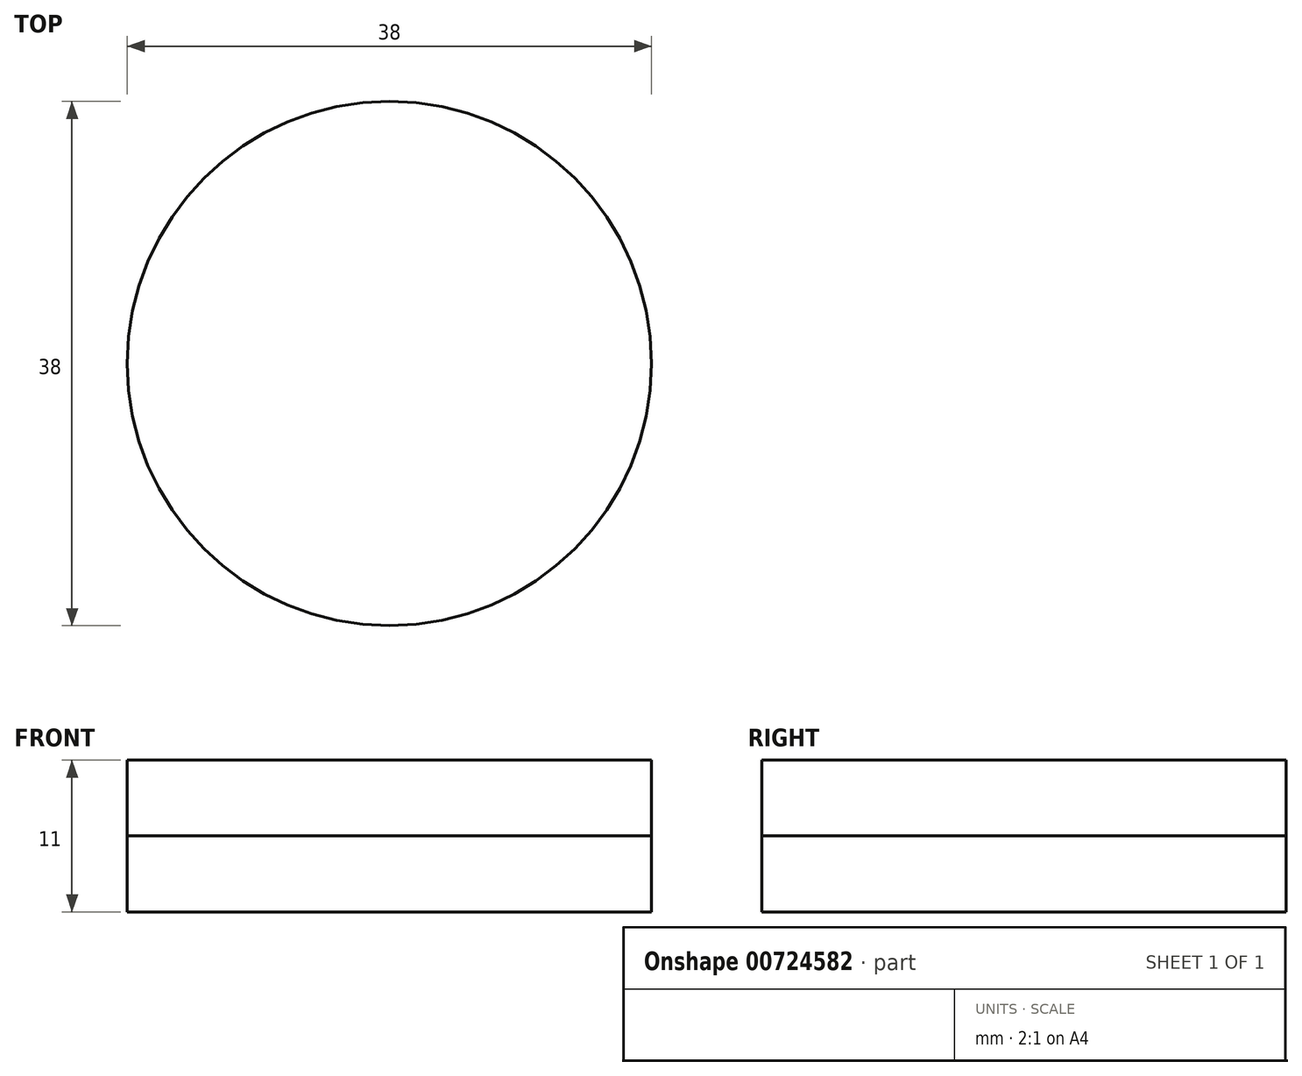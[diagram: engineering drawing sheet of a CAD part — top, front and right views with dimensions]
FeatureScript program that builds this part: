
annotation { "Feature Type Name" : "Feature", "Feature Type Description" : "" }
export const myFeature = defineFeature(function(context is Context, id is Id, definition is map)
    precondition{}
    {
        {
            var Q0;
            Q0=qCreatedBy(makeId("Top.planeOp"),FACE);
            var sketch = newSketch(context, id + "F0", { "sketchPlane" : qUnion([Q0])});
            skCircle(sketch, "E0", {"center": v(0, 0) * mm, "radius": 19 * mm});
            skSolve(sketch);
        }
        {
            var Q0;
            Q0=makeQuery(id+"F0.imprint","IMPRINT",FACE,{"disambiguationData":[TD([[makeQuery(id+"F0.imprint","IMPRINT",EDGE,{"derivedFrom":sQuery(id+"F0.wireOp",EDGE,"E0")}),1.0]])]});
            extrude(context, id + "F1", {"entities" : qUnion([Q0]), "depth" : 5.5 * mm, "offsetDistance" : 25 * mm});
        }
        {
            var Q0;
            Q0=makeQuery(id+"F1.opExtrude","CAP_FACE",FACE,{"disambiguationData":[OSD([sQuery(id+"F0.wireOp",EDGE,"E0")])],"isStart":true});
            extrude(context, id + "F2", {"entities" : qUnion([Q0]), "depth" : 5.5 * mm, "offsetDistance" : 25 * mm});
        }
    });
